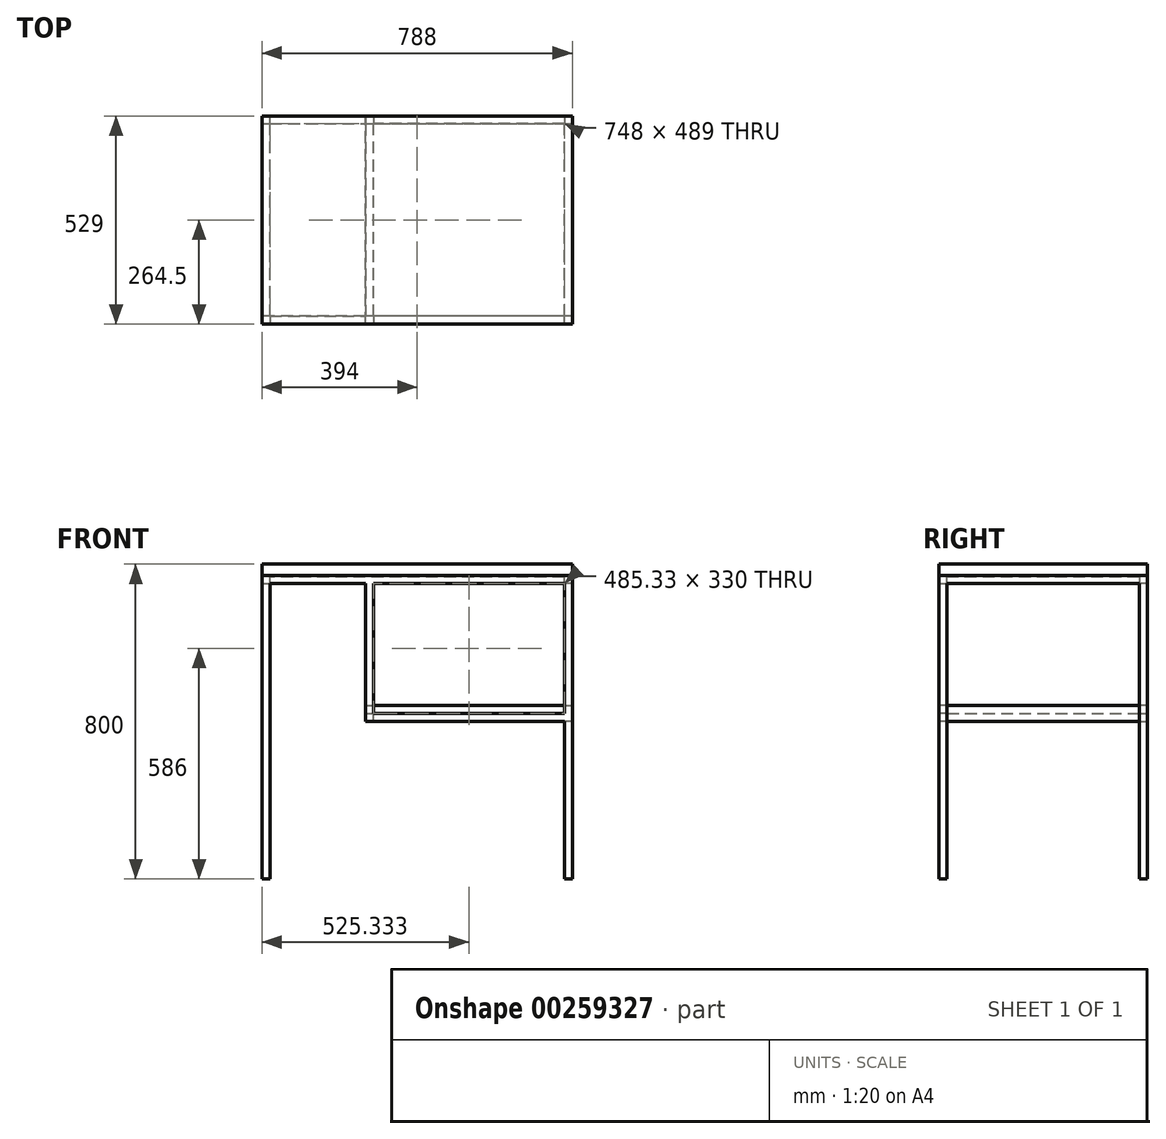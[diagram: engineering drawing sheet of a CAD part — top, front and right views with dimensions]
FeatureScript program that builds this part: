
annotation { "Feature Type Name" : "Feature", "Feature Type Description" : "" }
export const myFeature = defineFeature(function(context is Context, id is Id, definition is map)
    precondition{}
    {
        {
            assignVariable(context, id + "F0", {"name" : "epaisseur_top", "anyValue" : 33});
        }
        {
            assignVariable(context, id + "F1", {"name" : "profondeur", "anyValue" : 529});
        }
        {
            assignVariable(context, id + "F2", {"name" : "hauteur", "anyValue" : 800});
        }
        {
            assignVariable(context, id + "F3", {"name" : "enfoncement_top", "anyValue" : 4});
        }
        {
            var Q0;
            Q0=qCreatedBy(makeId("Top.planeOp"),FACE);
            var sketch = newSketch(context, id + "F4", { "sketchPlane" : qUnion([Q0])});
            skLineSegment(sketch, "E0.bottom", {"start": v(-394, 264.5) * mm, "end": v(-374, 264.5) * mm});
            skLineSegment(sketch, "E0.top", {"start": v(-394, 244.5) * mm, "end": v(-374, 244.5) * mm});
            skLineSegment(sketch, "E0.left", {"start": v(-394, 264.5) * mm, "end": v(-394, 244.5) * mm});
            skLineSegment(sketch, "E0.right", {"start": v(-374, 264.5) * mm, "end": v(-374, 244.5) * mm});
            skLineSegment(sketch, "E1.MirrorCS", {"start": v(394, 264.5) * mm, "end": v(374, 264.5) * mm});
            skLineSegment(sketch, "E2.MirrorCS", {"start": v(394, 244.5) * mm, "end": v(374, 244.5) * mm});
            skLineSegment(sketch, "E3.MirrorCS", {"start": v(374, 264.5) * mm, "end": v(374, 244.5) * mm});
            skLineSegment(sketch, "E4.MirrorCS", {"start": v(394, 264.5) * mm, "end": v(394, 244.5) * mm});
            skLineSegment(sketch, "E5.MirrorCS", {"start": v(394, -264.5) * mm, "end": v(394, -244.5) * mm});
            skLineSegment(sketch, "E6.MirrorCS", {"start": v(-394, -264.5) * mm, "end": v(-374, -264.5) * mm});
            skLineSegment(sketch, "E7.MirrorCS", {"start": v(-394, -244.5) * mm, "end": v(-374, -244.5) * mm});
            skLineSegment(sketch, "E8.MirrorCS", {"start": v(-394, -264.5) * mm, "end": v(-394, -244.5) * mm});
            skLineSegment(sketch, "E9.MirrorCS", {"start": v(-374, -264.5) * mm, "end": v(-374, -244.5) * mm});
            skLineSegment(sketch, "E10.MirrorCS", {"start": v(394, -264.5) * mm, "end": v(374, -264.5) * mm});
            skLineSegment(sketch, "E11.MirrorCS", {"start": v(394, -244.5) * mm, "end": v(374, -244.5) * mm});
            skLineSegment(sketch, "E12.MirrorCS", {"start": v(374, -264.5) * mm, "end": v(374, -244.5) * mm});
            skSolve(sketch);
        }
        {
            var Q0;
            Q0 = qSketchRegion(id + "F4", true);
            extrude(context, id + "F5", {"entities" : qUnion([Q0]), "depth" : (getVariable(context, 'hauteur') - getVariable(context, 'epaisseur_top') + getVariable(context, 'enfoncement_top')) * mm});
        }
        {
            var Q0;
            Q0=makeQuery(id+"F5.opExtrude","SWEPT_FACE",FACE,{"disambiguationData":[OSD([sQuery(id+"F4.wireOp",EDGE,"E3.MirrorCS")])]});
            var sketch = newSketch(context, id + "F6", { "sketchPlane" : qUnion([Q0])});
            skLineSegment(sketch, "E13.bottom", {"start": v(-264.5, 771) * mm, "end": v(-244.5, 771) * mm});
            skLineSegment(sketch, "E13.top", {"start": v(-264.5, 751) * mm, "end": v(-244.5, 751) * mm});
            skLineSegment(sketch, "E13.left", {"start": v(-264.5, 771) * mm, "end": v(-264.5, 751) * mm});
            skLineSegment(sketch, "E13.right", {"start": v(-244.5, 771) * mm, "end": v(-244.5, 751) * mm});
            skSolve(sketch);
        }
        {
            var Q0;
            Q0 = qSketchRegion(id + "F6", true);
            extrude(context, id + "F7", {"entities" : qUnion([Q0]), "endBound" : BoundingType.UP_TO_NEXT, "depth" : 25 * mm});
        }
        {
            var Q0;
            Q0=makeQuery(id+"F7.opExtrude","SWEPT_BODY",BODY,{"disambiguationData":[OSD([sQuery(id+"F6.wireOp",EDGE,"E13.bottom"),sQuery(id+"F6.wireOp",EDGE,"E13.top"),sQuery(id+"F6.wireOp",EDGE,"E13.left"),sQuery(id+"F6.wireOp",EDGE,"E13.right")])]});
            var Q1;
            Q1=qCreatedBy(makeId("Front.planeOp"),FACE);
            mirror(context, id + "F8", {"entities" : qUnion([Q0]), "mirrorPlane" : qUnion([Q1])});
        }
        {
            var Q0;
            Q0=makeQuery(id+"F5.opExtrude","SWEPT_FACE",FACE,{"disambiguationData":[OSD([sQuery(id+"F4.wireOp",EDGE,"E0.top")])]});
            var sketch = newSketch(context, id + "F9", { "sketchPlane" : qUnion([Q0])});
            skLineSegment(sketch, "E14.bottom", {"start": v(-394, 771) * mm, "end": v(-374, 771) * mm});
            skLineSegment(sketch, "E14.top", {"start": v(-394, 751) * mm, "end": v(-374, 751) * mm});
            skLineSegment(sketch, "E14.left", {"start": v(-394, 771) * mm, "end": v(-394, 751) * mm});
            skLineSegment(sketch, "E14.right", {"start": v(-374, 771) * mm, "end": v(-374, 751) * mm});
            skSolve(sketch);
        }
        {
            var Q0;
            Q0 = qSketchRegion(id + "F9", true);
            extrude(context, id + "F10", {"entities" : qUnion([Q0]), "endBound" : BoundingType.UP_TO_NEXT, "depth" : 25 * mm});
        }
        {
            var Q0;
            Q0=makeQuery(id+"F10.opExtrude","SWEPT_BODY",BODY,{"disambiguationData":[OSD([sQuery(id+"F9.wireOp",EDGE,"E14.bottom"),sQuery(id+"F9.wireOp",EDGE,"E14.top"),sQuery(id+"F9.wireOp",EDGE,"E14.left"),sQuery(id+"F9.wireOp",EDGE,"E14.right")])]});
            var Q1;
            Q1=qCreatedBy(makeId("Right.planeOp"),FACE);
            mirror(context, id + "F11", {"entities" : qUnion([Q0]), "mirrorPlane" : qUnion([Q1])});
        }
        {
            var Q0;
            Q0=makeQuery(id+"F5.opExtrude","SWEPT_BODY",BODY,{"disambiguationData":[OSD([sQuery(id+"F4.wireOp",EDGE,"E0.left"),sQuery(id+"F4.wireOp",EDGE,"E0.right"),sQuery(id+"F4.wireOp",EDGE,"E0.top"),sQuery(id+"F4.wireOp",EDGE,"E0.bottom")])]});
            var Q1;
            Q1=makeQuery(id+"F11.opPattern","COPY",BODY,{"derivedFrom":makeQuery(id+"F10.opExtrude","SWEPT_BODY",BODY,{"disambiguationData":[OSD([sQuery(id+"F9.wireOp",EDGE,"E14.bottom"),sQuery(id+"F9.wireOp",EDGE,"E14.top"),sQuery(id+"F9.wireOp",EDGE,"E14.left"),sQuery(id+"F9.wireOp",EDGE,"E14.right")])]}),"instanceName":"1"});
            var Q2;
            Q2=makeQuery(id+"F5.opExtrude","SWEPT_BODY",BODY,{"disambiguationData":[OSD([sQuery(id+"F4.wireOp",EDGE,"E1.MirrorCS"),sQuery(id+"F4.wireOp",EDGE,"E3.MirrorCS"),sQuery(id+"F4.wireOp",EDGE,"E4.MirrorCS"),sQuery(id+"F4.wireOp",EDGE,"E2.MirrorCS")])]});
            var Q3;
            Q3=makeQuery(id+"F10.opExtrude","SWEPT_BODY",BODY,{"disambiguationData":[OSD([sQuery(id+"F9.wireOp",EDGE,"E14.bottom"),sQuery(id+"F9.wireOp",EDGE,"E14.top"),sQuery(id+"F9.wireOp",EDGE,"E14.left"),sQuery(id+"F9.wireOp",EDGE,"E14.right")])]});
            var Q4;
            Q4=makeQuery(id+"F5.opExtrude","SWEPT_BODY",BODY,{"disambiguationData":[OSD([sQuery(id+"F4.wireOp",EDGE,"E11.MirrorCS"),sQuery(id+"F4.wireOp",EDGE,"E5.MirrorCS"),sQuery(id+"F4.wireOp",EDGE,"E12.MirrorCS"),sQuery(id+"F4.wireOp",EDGE,"E10.MirrorCS")])]});
            var Q5;
            Q5=makeQuery(id+"F8.opPattern","COPY",BODY,{"derivedFrom":makeQuery(id+"F7.opExtrude","SWEPT_BODY",BODY,{"disambiguationData":[OSD([sQuery(id+"F6.wireOp",EDGE,"E13.bottom"),sQuery(id+"F6.wireOp",EDGE,"E13.top"),sQuery(id+"F6.wireOp",EDGE,"E13.left"),sQuery(id+"F6.wireOp",EDGE,"E13.right")])]}),"instanceName":"1"});
            var Q6;
            Q6=makeQuery(id+"F7.opExtrude","SWEPT_BODY",BODY,{"disambiguationData":[OSD([sQuery(id+"F6.wireOp",EDGE,"E13.bottom"),sQuery(id+"F6.wireOp",EDGE,"E13.top"),sQuery(id+"F6.wireOp",EDGE,"E13.left"),sQuery(id+"F6.wireOp",EDGE,"E13.right")])]});
            var Q7;
            Q7=makeQuery(id+"F5.opExtrude","SWEPT_BODY",BODY,{"disambiguationData":[OSD([sQuery(id+"F4.wireOp",EDGE,"E6.MirrorCS"),sQuery(id+"F4.wireOp",EDGE,"E7.MirrorCS"),sQuery(id+"F4.wireOp",EDGE,"E8.MirrorCS"),sQuery(id+"F4.wireOp",EDGE,"E9.MirrorCS")])]});
            booleanBodies(context, id + "F12", {"operationType" : BooleanOperationType.UNION, "tools" : qUnion([Q0, Q1, Q2, Q3, Q4, Q5, Q6, Q7])});
        }
        {
            var Q0;
            {var subQ0=makeQuery(id+"F10.opExtrude","SWEPT_FACE",FACE,{"disambiguationData":[OSD([sQuery(id+"F9.wireOp",EDGE,"E14.bottom")])]});var subQ1=makeQuery(id+"F7.opExtrude","SWEPT_FACE",FACE,{"disambiguationData":[OSD([sQuery(id+"F6.wireOp",EDGE,"E13.bottom")])]});Q0=makeQuery(id+"F12.opBoolean","MERGE",FACE,{"derivedFrom":[makeQuery(id+"F5.opExtrude","CAP_FACE",FACE,{"disambiguationData":[OSD([sQuery(id+"F4.wireOp",EDGE,"E0.left"),sQuery(id+"F4.wireOp",EDGE,"E0.right"),sQuery(id+"F4.wireOp",EDGE,"E0.top"),sQuery(id+"F4.wireOp",EDGE,"E0.bottom")])],"isStart":false}),makeQuery(id+"F5.opExtrude","CAP_FACE",FACE,{"disambiguationData":[OSD([sQuery(id+"F4.wireOp",EDGE,"E1.MirrorCS"),sQuery(id+"F4.wireOp",EDGE,"E3.MirrorCS"),sQuery(id+"F4.wireOp",EDGE,"E4.MirrorCS"),sQuery(id+"F4.wireOp",EDGE,"E2.MirrorCS")])],"isStart":false}),makeQuery(id+"F5.opExtrude","CAP_FACE",FACE,{"disambiguationData":[OSD([sQuery(id+"F4.wireOp",EDGE,"E11.MirrorCS"),sQuery(id+"F4.wireOp",EDGE,"E5.MirrorCS"),sQuery(id+"F4.wireOp",EDGE,"E12.MirrorCS"),sQuery(id+"F4.wireOp",EDGE,"E10.MirrorCS")])],"isStart":false}),makeQuery(id+"F5.opExtrude","CAP_FACE",FACE,{"disambiguationData":[OSD([sQuery(id+"F4.wireOp",EDGE,"E6.MirrorCS"),sQuery(id+"F4.wireOp",EDGE,"E7.MirrorCS"),sQuery(id+"F4.wireOp",EDGE,"E8.MirrorCS"),sQuery(id+"F4.wireOp",EDGE,"E9.MirrorCS")])],"isStart":false}),subQ1,makeQuery(id+"F8.opPattern","COPY",FACE,{"derivedFrom":subQ1,"instanceName":"1"}),subQ0,makeQuery(id+"F11.opPattern","COPY",FACE,{"derivedFrom":subQ0,"instanceName":"1"})]});}
            var sketch = newSketch(context, id + "F13", { "sketchPlane" : qUnion([Q0])});
            skLineSegment(sketch, "E15.bottom", {"start": v(-394, 264.5) * mm, "end": v(394, 264.5) * mm});
            skLineSegment(sketch, "E15.top", {"start": v(-394, -264.5) * mm, "end": v(394, -264.5) * mm});
            skLineSegment(sketch, "E15.left", {"start": v(-394, 264.5) * mm, "end": v(-394, -264.5) * mm});
            skLineSegment(sketch, "E15.right", {"start": v(394, 264.5) * mm, "end": v(394, -264.5) * mm});
            skSolve(sketch);
        }
        {
            var Q0;
            Q0 = qSketchRegion(id + "F13", true);
            extrude(context, id + "F14", {"entities" : qUnion([Q0]), "depth" : (getVariable(context, 'epaisseur_top') - getVariable(context, 'enfoncement_top')) * mm, "hasSecondDirection" : true, "secondDirectionOppositeDirection" : true, "secondDirectionDepth" : (getVariable(context, 'enfoncement_top')) * mm});
        }
        {
            var Q0;
            Q0=makeQuery(id+"F5.opExtrude","SWEPT_BODY",BODY,{"disambiguationData":[OSD([sQuery(id+"F4.wireOp",EDGE,"E0.left"),sQuery(id+"F4.wireOp",EDGE,"E0.right"),sQuery(id+"F4.wireOp",EDGE,"E0.top"),sQuery(id+"F4.wireOp",EDGE,"E0.bottom")])]});
            var Q1;
            Q1=makeQuery(id+"F14.opExtrude","SWEPT_BODY",BODY,{"disambiguationData":[OSD([sQuery(id+"F13.wireOp",EDGE,"E15.bottom"),sQuery(id+"F13.wireOp",EDGE,"E15.top"),sQuery(id+"F13.wireOp",EDGE,"E15.left"),sQuery(id+"F13.wireOp",EDGE,"E15.right")])]});
            booleanBodies(context, id + "F15", {"operationType" : BooleanOperationType.SUBTRACTION, "tools" : qUnion([Q0]), "targets" : qUnion([Q1]), "keepTools" : true});
        }
        {
            var Q0;
            Q0=makeQuery(id+"F8.opPattern","COPY",FACE,{"derivedFrom":makeQuery(id+"F7.opExtrude","SWEPT_FACE",FACE,{"disambiguationData":[OSD([sQuery(id+"F6.wireOp",EDGE,"E13.top")])]}),"instanceName":"1"});
            var sketch = newSketch(context, id + "F16", { "sketchPlane" : qUnion([Q0])});
            skLineSegment(sketch, "E16.bottom", {"start": v(-131.33, 264.5) * mm, "end": v(-111.33, 264.5) * mm});
            skLineSegment(sketch, "E16.top", {"start": v(-131.33, 244.5) * mm, "end": v(-111.33, 244.5) * mm});
            skLineSegment(sketch, "E16.left", {"start": v(-131.33, 264.5) * mm, "end": v(-131.33, 244.5) * mm});
            skLineSegment(sketch, "E16.right", {"start": v(-111.33, 264.5) * mm, "end": v(-111.33, 244.5) * mm});
            skSolve(sketch);
        }
        {
            var Q0;
            Q0 = qSketchRegion(id + "F16", true);
            extrude(context, id + "F17", {"entities" : qUnion([Q0]), "depth" : 350 * mm, "offsetDistance" : 25 * mm});
        }
        {
            var Q0;
            Q0=makeQuery(id+"F17.opExtrude","SWEPT_FACE",FACE,{"disambiguationData":[OSD([sQuery(id+"F16.wireOp",EDGE,"E16.right")])]});
            var sketch = newSketch(context, id + "F18", { "sketchPlane" : qUnion([Q0])});
            skLineSegment(sketch, "E17.bottom", {"start": v(-264.5, 401) * mm, "end": v(-244.5, 401) * mm});
            skLineSegment(sketch, "E17.top", {"start": v(-264.5, 421) * mm, "end": v(-244.5, 421) * mm});
            skLineSegment(sketch, "E17.left", {"start": v(-264.5, 401) * mm, "end": v(-264.5, 421) * mm});
            skLineSegment(sketch, "E17.right", {"start": v(-244.5, 401) * mm, "end": v(-244.5, 421) * mm});
            skSolve(sketch);
        }
        {
            var Q0;
            Q0=makeQuery(id+"F18.imprint","IMPRINT",FACE,{"disambiguationData":[TD([[makeQuery(id+"F18.imprint","IMPRINT",EDGE,{"derivedFrom":sQuery(id+"F18.wireOp",EDGE,"E17.bottom")}),1.0]])]});
            extrude(context, id + "F19", {"entities" : qUnion([Q0]), "endBound" : BoundingType.UP_TO_NEXT, "depth" : 25 * mm});
        }
        {
            var Q0;
            Q0=makeQuery(id+"F17.opExtrude","SWEPT_BODY",BODY,{"disambiguationData":[OSD([sQuery(id+"F16.wireOp",EDGE,"E16.bottom"),sQuery(id+"F16.wireOp",EDGE,"E16.top"),sQuery(id+"F16.wireOp",EDGE,"E16.left"),sQuery(id+"F16.wireOp",EDGE,"E16.right")])]});
            var Q1;
            Q1=makeQuery(id+"F19.opExtrude","SWEPT_BODY",BODY,{"disambiguationData":[OSD([sQuery(id+"F18.wireOp",EDGE,"E17.bottom"),sQuery(id+"F18.wireOp",EDGE,"E17.top"),sQuery(id+"F18.wireOp",EDGE,"E17.left"),sQuery(id+"F18.wireOp",EDGE,"E17.right")])]});
            var Q2;
            Q2=qCreatedBy(makeId("Front.planeOp"),FACE);
            mirror(context, id + "F20", {"operationType" : NewBodyOperationType.ADD, "entities" : qUnion([Q0, Q1]), "mirrorPlane" : qUnion([Q2])});
        }
        {
            var Q0;
            {var subQ0=makeQuery(id+"F7.opExtrude","SWEPT_FACE",FACE,{"disambiguationData":[OSD([sQuery(id+"F6.wireOp",EDGE,"E13.right")])]});var subQ1=makeQuery(id+"F5.opExtrude","SWEPT_FACE",FACE,{"disambiguationData":[OSD([sQuery(id+"F4.wireOp",EDGE,"E2.MirrorCS")])]});Q0=makeQuery(id+"F20.boolean.opBoolean","MERGE",FACE,{"derivedFrom":[makeQuery(id+"F12.opBoolean","MERGE",FACE,{"derivedFrom":[subQ1,subQ0]}),makeQuery(id+"F12.opBoolean","MERGE",FACE,{"disambiguationData":[OD(1.0)],"derivedFrom":[makeQuery(id+"F5.opExtrude","SWEPT_FACE",FACE,{"disambiguationData":[OSD([sQuery(id+"F4.wireOp",EDGE,"E0.top")])]}),subQ1,subQ0]}),makeQuery(id+"F20.opPattern","COPY",FACE,{"derivedFrom":makeQuery(id+"F17.opExtrude","SWEPT_FACE",FACE,{"disambiguationData":[OSD([sQuery(id+"F16.wireOp",EDGE,"E16.top")])]}),"instanceName":"1"}),makeQuery(id+"F20.opPattern","COPY",FACE,{"derivedFrom":makeQuery(id+"F19.opExtrude","SWEPT_FACE",FACE,{"disambiguationData":[OSD([sQuery(id+"F18.wireOp",EDGE,"E17.right")])]}),"instanceName":"1"})]});}
            var sketch = newSketch(context, id + "F21", { "sketchPlane" : qUnion([Q0])});
            skLineSegment(sketch, "E18.bottom", {"start": v(-131.33, 401) * mm, "end": v(-111.33, 401) * mm});
            skLineSegment(sketch, "E18.top", {"start": v(-131.33, 421) * mm, "end": v(-111.33, 421) * mm});
            skLineSegment(sketch, "E18.left", {"start": v(-131.33, 401) * mm, "end": v(-131.33, 421) * mm});
            skLineSegment(sketch, "E18.right", {"start": v(-111.33, 401) * mm, "end": v(-111.33, 421) * mm});
            skSolve(sketch);
        }
        {
            var Q0;
            Q0 = qSketchRegion(id + "F21", true);
            extrude(context, id + "F22", {"entities" : qUnion([Q0]), "operationType" : NewBodyOperationType.ADD, "endBound" : BoundingType.UP_TO_NEXT, "depth" : 25 * mm});
        }
        {
            var Q0;
            Q0=makeQuery(id+"F20.boolean.opBoolean","MERGE",FACE,{"derivedFrom":[makeQuery(id+"F12.opBoolean","MERGE",FACE,{"derivedFrom":[makeQuery(id+"F5.opExtrude","SWEPT_FACE",FACE,{"disambiguationData":[OSD([sQuery(id+"F4.wireOp",EDGE,"E6.MirrorCS")])]}),makeQuery(id+"F5.opExtrude","SWEPT_FACE",FACE,{"disambiguationData":[OSD([sQuery(id+"F4.wireOp",EDGE,"E10.MirrorCS")])]}),makeQuery(id+"F8.opPattern","COPY",FACE,{"derivedFrom":makeQuery(id+"F7.opExtrude","SWEPT_FACE",FACE,{"disambiguationData":[OSD([sQuery(id+"F6.wireOp",EDGE,"E13.left")])]}),"instanceName":"1"})]}),makeQuery(id+"F17.opExtrude","SWEPT_FACE",FACE,{"disambiguationData":[OSD([sQuery(id+"F16.wireOp",EDGE,"E16.bottom")])]}),makeQuery(id+"F19.opExtrude","SWEPT_FACE",FACE,{"disambiguationData":[OSD([sQuery(id+"F18.wireOp",EDGE,"E17.left")])]})]});
            var sketch = newSketch(context, id + "F23", { "sketchPlane" : qUnion([Q0])});
            skLineSegment(sketch, "E19.bottom", {"start": v(-131.33, 441) * mm, "end": v(394, 441) * mm});
            skLineSegment(sketch, "E19.top", {"start": v(-131.33, 401) * mm, "end": v(394, 401) * mm});
            skLineSegment(sketch, "E19.left", {"start": v(-131.33, 441) * mm, "end": v(-131.33, 401) * mm});
            skLineSegment(sketch, "E19.right", {"start": v(394, 441) * mm, "end": v(394, 401) * mm});
            skSolve(sketch);
        }
        {
            var Q0;
            Q0 = qSketchRegion(id + "F23", true);
            extrude(context, id + "F24", {"entities" : qUnion([Q0]), "oppositeDirection" : true, "depth" : (getVariable(context, 'profondeur')) * mm});
        }
        {
            var Q0;
            Q0=makeQuery(id+"F5.opExtrude","SWEPT_BODY",BODY,{"disambiguationData":[OSD([sQuery(id+"F4.wireOp",EDGE,"E0.left"),sQuery(id+"F4.wireOp",EDGE,"E0.right"),sQuery(id+"F4.wireOp",EDGE,"E0.top"),sQuery(id+"F4.wireOp",EDGE,"E0.bottom")])]});
            var Q1;
            Q1=makeQuery(id+"F24.opExtrude","SWEPT_BODY",BODY,{"disambiguationData":[OSD([sQuery(id+"F23.wireOp",EDGE,"E19.bottom"),sQuery(id+"F23.wireOp",EDGE,"E19.top"),sQuery(id+"F23.wireOp",EDGE,"E19.left"),sQuery(id+"F23.wireOp",EDGE,"E19.right")])]});
            booleanBodies(context, id + "F25", {"operationType" : BooleanOperationType.SUBTRACTION, "tools" : qUnion([Q0]), "targets" : qUnion([Q1]), "keepTools" : true});
        }
    });
